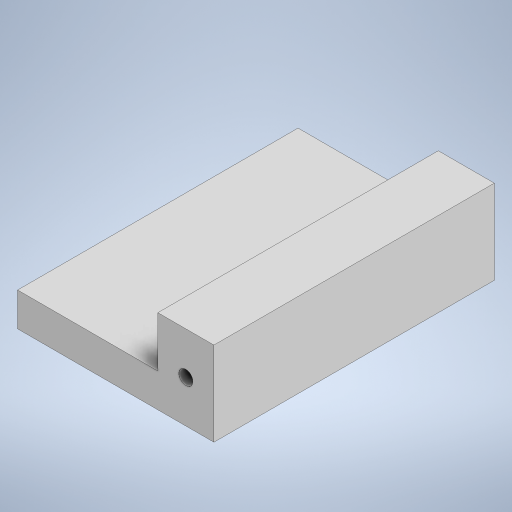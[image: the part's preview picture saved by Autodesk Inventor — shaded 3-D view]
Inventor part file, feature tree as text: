
AUTODESK INVENTOR PART (.ipt)
format: ipt  version: 2023 (Build 270158000, 158)  size: 240,640 bytes
history: native  units: in
note: dims shown in document units (in); Inventor stores cm internally (conversion verified against a paired STEP export)
features: extrude x3, sketch x3
ambient origin geometry x8: Origin, YZ Plane, XZ Plane, XY Plane, X Axis, Y Axis, Z Axis, Center Point
bodies: Body1 (feature_tree)
feature tree (6):
  extrude  "Extrusion2"  Depth=0.7874in
  extrude  "Extrusion4"  Depth=0.3937in
  extrude  "Extrusion5"  Depth=0.9843in TaperAngle=0.0deg
  sketch  "Sketch1"  dims[d0=1.1811in d1=0.7874in]
  sketch  "Sketch4"  dims[d5=0.3937in d6=0.5906in]
  sketch  "Sketch5"  dims[d7=0.1969in d8=0.9843in d9=0.0in d13=0.4724in d14=1.9685in d15=3.937in d16=0.0in d17=0.3543in d18=2.9528in d19=0.0in]
